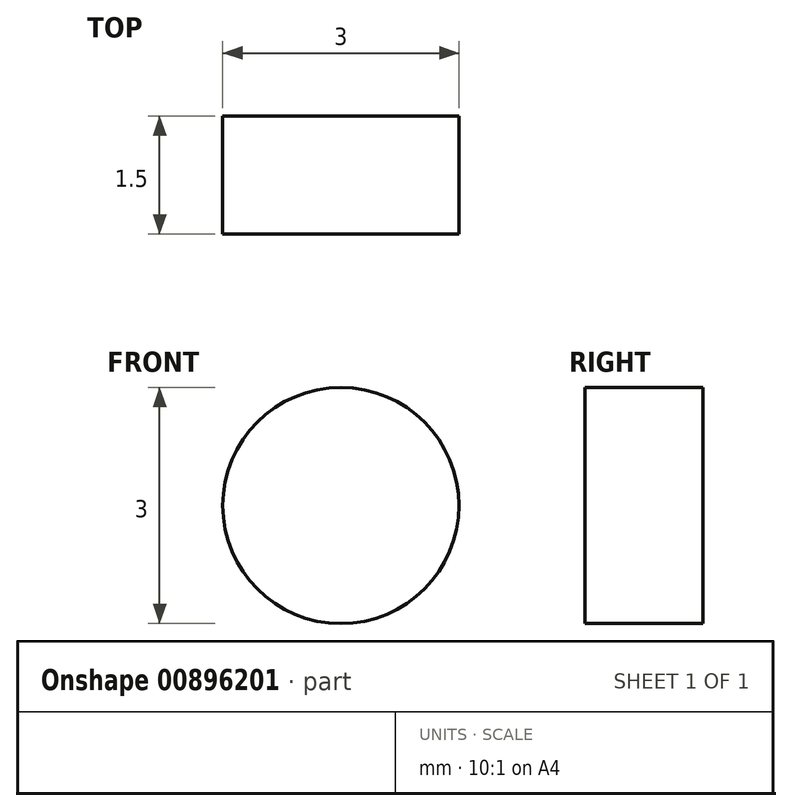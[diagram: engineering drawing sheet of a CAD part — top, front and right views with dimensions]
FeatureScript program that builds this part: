
annotation { "Feature Type Name" : "Feature", "Feature Type Description" : "" }
export const myFeature = defineFeature(function(context is Context, id is Id, definition is map)
    precondition{}
    {
        {
            var Q0;
            Q0=qCreatedBy(makeId("Front.planeOp"),FACE);
            var sketch = newSketch(context, id + "F0", { "sketchPlane" : qUnion([Q0])});
            skCircle(sketch, "E0", {"center": v(0, 0) * mm, "radius": 1.5 * mm});
            skSolve(sketch);
        }
        {
            var Q0;
            Q0=makeQuery(id+"F0.imprint","IMPRINT",FACE,{"disambiguationData":[TD([[makeQuery(id+"F0.imprint","IMPRINT",EDGE,{"derivedFrom":sQuery(id+"F0.wireOp",EDGE,"E0")}),1.0]])]});
            extrude(context, id + "F1", {"entities" : qUnion([Q0]), "depth" : 1.5 * mm, "offsetDistance" : 25 * mm});
        }
    });
